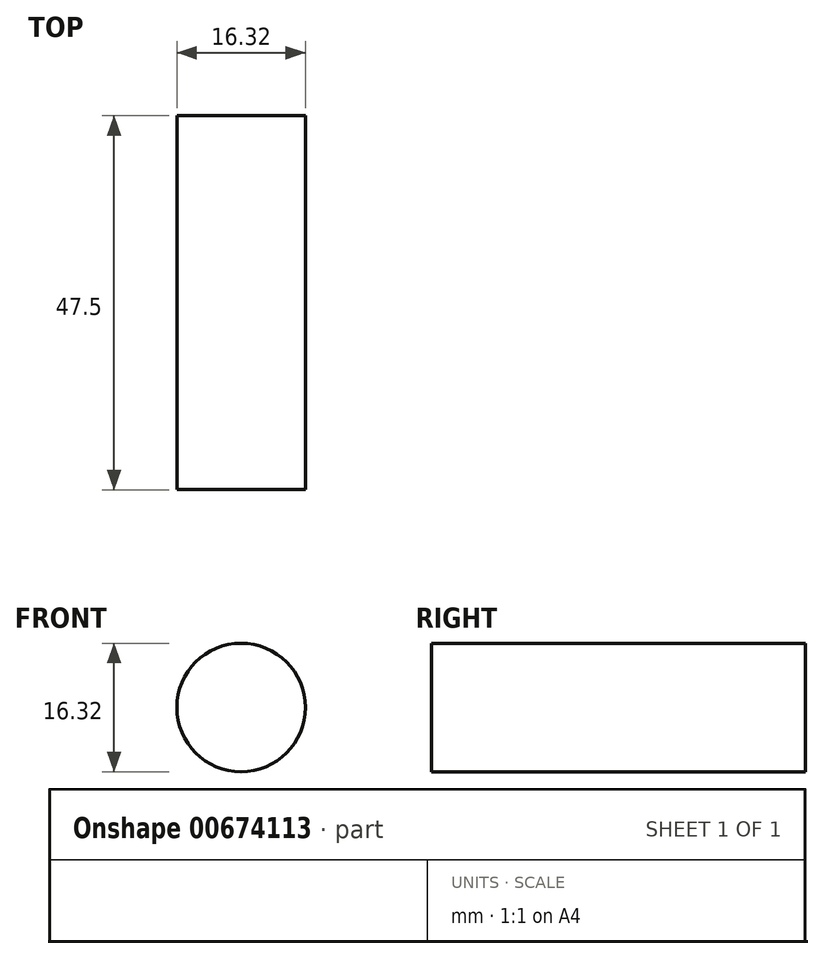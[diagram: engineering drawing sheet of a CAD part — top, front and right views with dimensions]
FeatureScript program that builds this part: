
annotation { "Feature Type Name" : "Feature", "Feature Type Description" : "" }
export const myFeature = defineFeature(function(context is Context, id is Id, definition is map)
    precondition{}
    {
        {
            var Q0;
            Q0=qCreatedBy(makeId("Right.planeOp"),FACE);
            var sketch = newSketch(context, id + "F0", { "sketchPlane" : qUnion([Q0])});
            skFitSpline(sketch, "E0", {"points": [v(-44.73, 0.3) * mm, v(120.37, -4.33) * mm, v(76.17, -2.44) * mm], "startDerivative": vector(341.02, 134.57) * mm, "endDerivative": vector(-12.39, 4.25) * mm});
            skFitSpline(sketch, "E1", {"points": [v(-44.73, 0.3) * mm, v(-73.24, -11.98) * mm, v(77.57, -2.92) * mm], "startDerivative": vector(543.35, -3.9) * mm, "endDerivative": vector(326.65, 32.34) * mm});
            skLineSegment(sketch, "E2", {"start": v(-50.66, -4.57) * mm, "end": v(0, 0) * mm});
            skSolve(sketch);
        }
        {
            var Q0;
            Q0=sQuery(id+"F0.wireOp",EDGE,"E1");
            var Q1;
            Q1=sQuery(id+"F0.wireOp",EDGE,"E0");
            extrude(context, id + "F1", {"bodyType" : ToolBodyType.SURFACE, "surfaceEntities" : qUnion([Q0, Q1]), "depth" : 25.4 * mm, "offsetDistance" : 25.4 * mm});
        }
        {
            var Q0;
            Q0=qCreatedBy(makeId("Front.planeOp"),FACE);
            var sketch = newSketch(context, id + "F2", { "sketchPlane" : qUnion([Q0])});
            skCircle(sketch, "E3", {"center": v(12.6, -1.73) * mm, "radius": 8.16 * mm});
            skCircle(sketch, "E4", {"center": v(12.6, -1.73) * mm, "radius": 4.73 * mm});
            skSolve(sketch);
        }
        {
            var Q0;
            Q0=makeQuery(id+"F2.imprint","IMPRINT",FACE,{"disambiguationData":[TD([[makeQuery(id+"F2.imprint","IMPRINT",EDGE,{"derivedFrom":sQuery(id+"F2.wireOp",EDGE,"E3")}),1.0]])]});
            var Q1;
            Q1=makeQuery(id+"F2.imprint","IMPRINT",FACE,{"disambiguationData":[TD([[makeQuery(id+"F2.imprint","IMPRINT",EDGE,{"derivedFrom":sQuery(id+"F2.wireOp",EDGE,"E4")}),1.0]])]});
            extrude(context, id + "F3", {"entities" : qUnion([Q0, Q1]), "depth" : 47.5 * mm, "offsetDistance" : 25.4 * mm});
        }
    });
